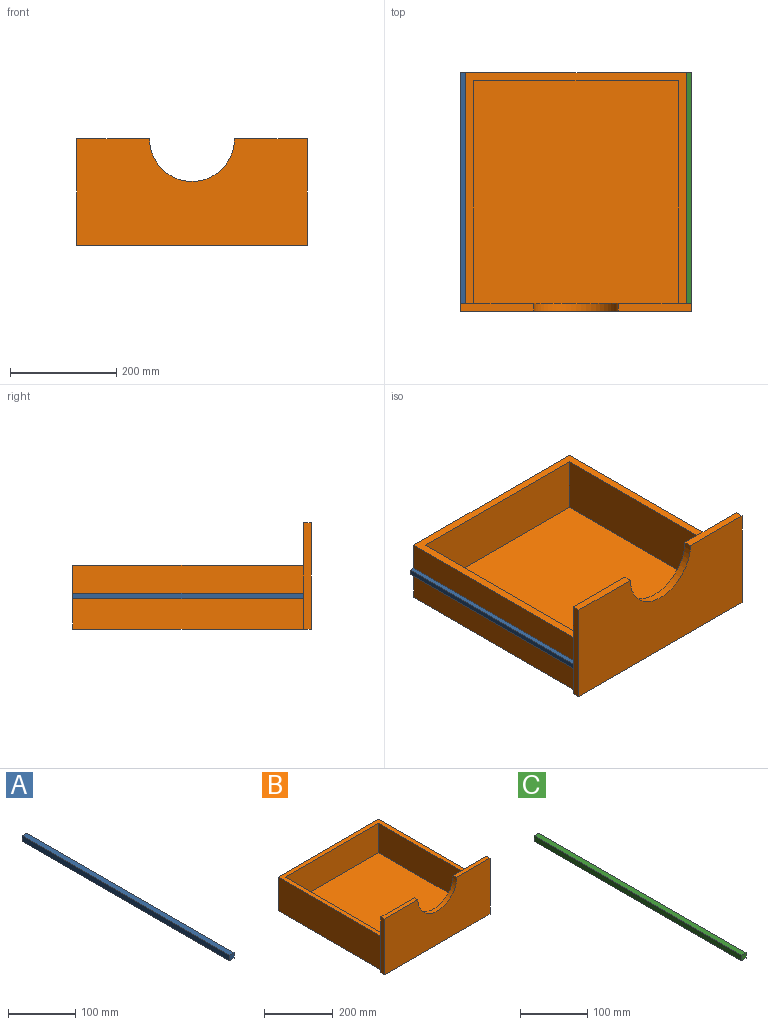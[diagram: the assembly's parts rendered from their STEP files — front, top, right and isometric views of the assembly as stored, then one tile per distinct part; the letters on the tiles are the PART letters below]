
ASSEMBLY  parts=3 mates=2
PART A: 6 faces, bbox 10x435x10 mm
  f0: plane 10x10mm, normal (0,-1,0), area 100mm2, adj f1,f3,f4,f5
  f1: plane 435x10mm, normal (0,0,-1), area 4350mm2, adj f0,f2,f4,f5
  f2: plane 10x10mm, normal (0,1,0), area 100mm2, adj f1,f3,f4,f5
  f3: plane 435x10mm, normal (0,0,1), area 4350mm2, adj f0,f2,f4,f5
  f4: plane 435x10mm, normal (-1,0,0), area 4350mm2, adj f0,f1,f2,f3
  f5: plane 435x10mm, normal (1,0,0), area 4350mm2, adj f0,f1,f2,f3
PART B: 16 faces, bbox 435x450x200 mm
  f0: plane 420x385mm, normal (0,0,1), area 161700mm2, adj f1,f12,f14,f15
  f1: plane 435x200mm, normal (0,1,0), area 67571.9mm2, adj f0,f2,f3,f4,f5,f6,f7,f9
  f2: plane 137.5x15mm, normal (0,0,1), area 2062.5mm2, adj f1,f3,f7,f8
  f3: plane 200x15mm, normal (-1,0,0), area 3000mm2, adj f1,f2,f4,f8
  f4: plane 450x435mm, normal (0,0,-1), area 187050mm2, adj f1,f3,f5,f8,f9,f10,f11
  f5: plane 200x15mm, normal (1,0,0), area 3000mm2, adj f1,f4,f6,f8
  f6: plane 137.5x15mm, normal (0,0,1), area 2062.5mm2, adj f1,f5,f7,f8
  f7: cylinder r=80mm len=160mm, axis (0,1,0), area 3769.9mm2, adj f1,f2,f6,f8
  f8: plane 435x200mm, normal (0,-1,0), area 76946.9mm2, adj f2,f3,f4,f5,f6,f7
  f9: plane 435x120mm, normal (1,0,0), area 52200mm2, adj f1,f4,f11,f13
  f10: plane 435x120mm, normal (-1,0,0), area 52200mm2, adj f1,f4,f11,f13
  f11: plane 415x120mm, normal (0,1,0), area 49800mm2, adj f4,f9,f10,f13
  f12: plane 420x105mm, normal (-1,0,0), area 44100mm2, adj f0,f1,f13,f15
  f13: plane 435x415mm, normal (0,0,1), area 18825mm2, adj f1,f9,f10,f11,f12,f14,f15
  f14: plane 420x105mm, normal (1,0,0), area 44100mm2, adj f0,f1,f13,f15
  f15: plane 385x105mm, normal (0,-1,0), area 40425mm2, adj f0,f12,f13,f14
PART C: 6 faces, bbox 10x435x10 mm
  f0: plane 10x10mm, normal (0,-1,0), area 100mm2, adj f1,f3,f4,f5
  f1: plane 435x10mm, normal (0,0,-1), area 4350mm2, adj f0,f2,f4,f5
  f2: plane 10x10mm, normal (0,1,0), area 100mm2, adj f1,f3,f4,f5
  f3: plane 435x10mm, normal (0,0,1), area 4350mm2, adj f0,f2,f4,f5
  f4: plane 435x10mm, normal (1,0,0), area 4350mm2, adj f0,f1,f2,f3
  f5: plane 435x10mm, normal (-1,0,0), area 4350mm2, adj f0,f1,f2,f3
PLACE A at identity fixed
PLACE B t=(0,0,-2.5)mm
PLACE C at identity
MATE fastened C.f3 <-> A.f3  axis (0,0,1) through (207.5,435,65)mm
MATE slider B.f11 <-> A.f2  axis (0,-1,0) through (-207.5,435,117.5)mm
